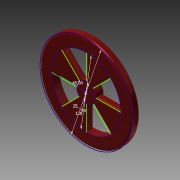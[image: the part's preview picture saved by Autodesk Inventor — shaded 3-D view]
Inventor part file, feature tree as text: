
AUTODESK INVENTOR PART (.ipt)
format: ipt  version: 2014 (Build 180170000, 170)  size: 202,752 bytes
history: native  units: mm
features: extrude x2, fillet x2, sketch x1
ambient origin geometry x8: Origin, YZ Plane, XZ Plane, XY Plane, X Axis, Y Axis, Z Axis, Center Point
bodies: Solid1 (feature_tree)
feature tree (5):
  sketch  "Sketch1"  dims[d0=6.0mm d1=120.0mm d2=10.0mm d3=0.0mm d4=25.0mm d5=90.0mm d7=45.0deg d8=10.0mm d9=0.0mm d10=3.0mm d11=3.0mm]
  extrude  "Extrusion1"  Depth=3.0mm
  extrude  "Extrusion2"  Depth=10.0mm TaperAngle=0.0deg
  fillet  "Fillet1"  Radius=25.0mm
  fillet  "Fillet2"  Radius=90.0mm
